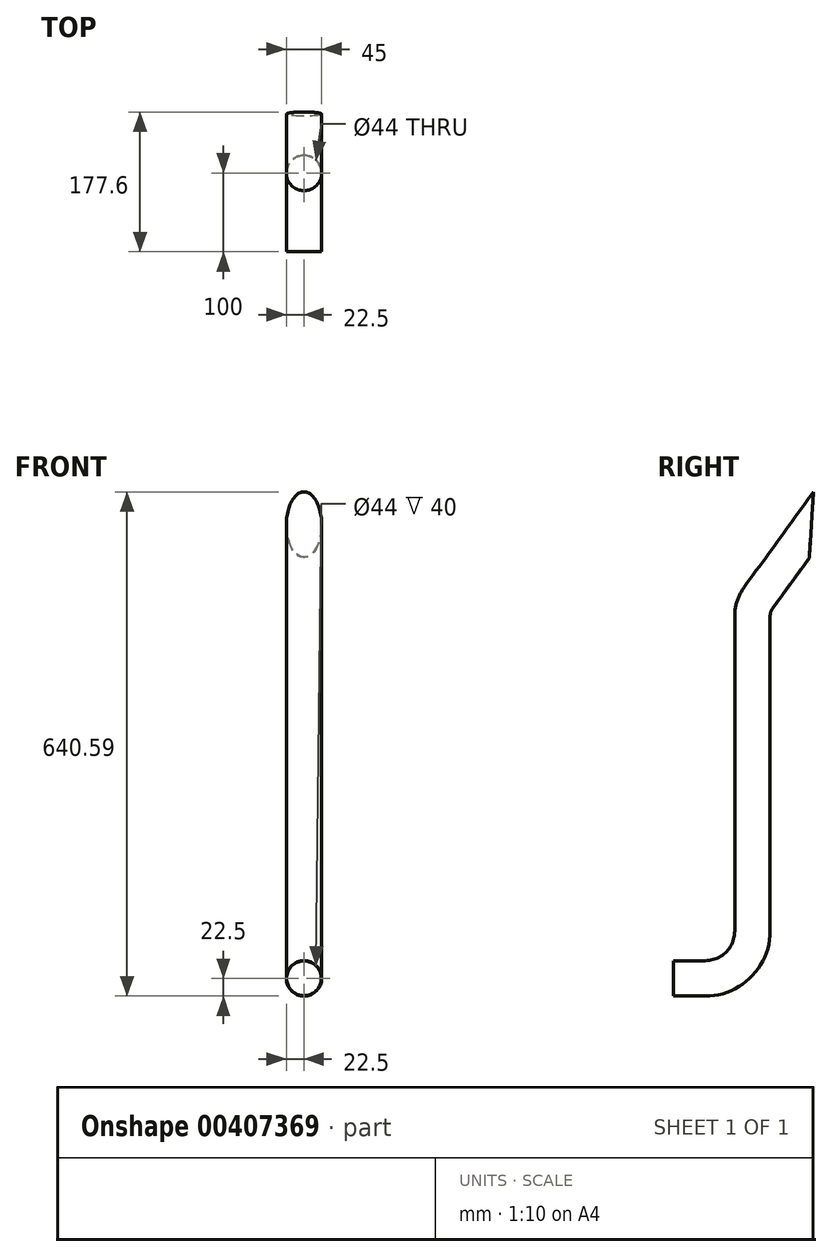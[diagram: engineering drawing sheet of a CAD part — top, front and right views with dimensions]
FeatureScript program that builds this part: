
annotation { "Feature Type Name" : "Feature", "Feature Type Description" : "" }
export const myFeature = defineFeature(function(context is Context, id is Id, definition is map)
    precondition{}
    {
        {
            var Q0;
            Q0=qCreatedBy(makeId("Right.planeOp"),FACE);
            var sketch = newSketch(context, id + "F0", { "sketchPlane" : qUnion([Q0])});
            skLineSegment(sketch, "E0", {"start": v(0, 0) * mm, "end": v(40, 0) * mm});
            skLineSegment(sketch, "E1", {"start": v(100, 60) * mm, "end": v(100, 460) * mm});
            skLineSegment(sketch, "E2", {"start": v(107.64, 483.51) * mm, "end": v(195.8, 604.86) * mm});
            skPoint(sketch, "E3.visualSharp", {"position": v(100, 0) * mm});
            skArc(sketch, "E3.filletArc", {"start": v(40, 0) * mm, "mid": v(82.43, 17.57) * mm, "end": v(100, 60) * mm});
            skPoint(sketch, "E4.visualSharp", {"position": v(100, 473) * mm});
            skArc(sketch, "E4.filletArc", {"start": v(107.64, 483.51) * mm, "mid": v(101.96, 472.36) * mm, "end": v(100, 460) * mm});
            skPoint(sketch, "E5.visualSharp", {"position": v(175.47, 576.87) * mm});
            skSolve(sketch);
        }
        {
            var Q0;
            Q0=qCreatedBy(makeId("Front.planeOp"),FACE);
            var sketch = newSketch(context, id + "F1", { "sketchPlane" : qUnion([Q0])});
            skCircle(sketch, "E6", {"center": v(0, 0) * mm, "radius": 22 * mm});
            skCircle(sketch, "E7", {"center": v(0, 0) * mm, "radius": 22.5 * mm});
            skSolve(sketch);
        }
        {
            var Q0;
            Q0=makeQuery(id+"F1.imprint","IMPRINT",FACE,{"disambiguationData":[TD([[makeQuery(id+"F1.imprint","IMPRINT",EDGE,{"derivedFrom":sQuery(id+"F1.wireOp",EDGE,"E6")}),-1.0]])]});
            var Q1;
            Q1=sQuery(id+"F0.wireOp",EDGE,"E0");
            var Q2;
            Q2=sQuery(id+"F0.wireOp",EDGE,"E3.filletArc");
            var Q3;
            Q3=sQuery(id+"F0.wireOp",EDGE,"E1");
            var Q4;
            Q4=sQuery(id+"F0.wireOp",EDGE,"E4.filletArc");
            var Q5;
            Q5=sQuery(id+"F0.wireOp",EDGE,"E2");
            var Q6;
            Q6=sQuery(id+"F0.wireOp",EDGE,"E5.filletArc");
            var Q7;
            Q7=sQuery(id+"F0.wireOp",EDGE,"ADRPB93s-L3ns-Njq6-n3NY-gjiRkliPrde4");
            sweep(context, id + "F2", {"profiles" : qUnion([Q0]), "path" : qUnion([Q1, Q2, Q3, Q4, Q5, Q6, Q7])});
        }
        {
            var Q0;
            Q0=qCreatedBy(makeId("Right.planeOp"),FACE);
            var sketch = newSketch(context, id + "F3", { "sketchPlane" : qUnion([Q0])});
            skLineSegment(sketch, "E8", {"start": v(145.31, 573.64) * mm, "end": v(177.6, 618.09) * mm});
            skLineSegment(sketch, "E9", {"start": v(214, 591.64) * mm, "end": v(130.36, 476.5) * mm});
            skLineSegment(sketch, "E10", {"start": v(177.6, 618.09) * mm, "end": v(172.19, 534.07) * mm});
            skLineSegment(sketch, "E11", {"start": v(172.19, 534.07) * mm, "end": v(214, 591.64) * mm});
            skLineSegment(sketch, "E12", {"start": v(177.6, 618.09) * mm, "end": v(214, 591.64) * mm});
            skSolve(sketch);
        }
        {
            var Q0;
            Q0=qSketchRegion(id+"F3",true);
            extrude(context, id + "F4", {"entities" : qUnion([Q0]), "operationType" : NewBodyOperationType.REMOVE, "endBound" : BoundingType.THROUGH_ALL, "depth" : 25 * mm});
        }
        {
            var Q0;
            Q0=qSketchRegion(id+"F3",true);
            extrude(context, id + "F5", {"entities" : qUnion([Q0]), "operationType" : NewBodyOperationType.REMOVE, "oppositeDirection" : true, "depth" : 25 * mm});
        }
    });
